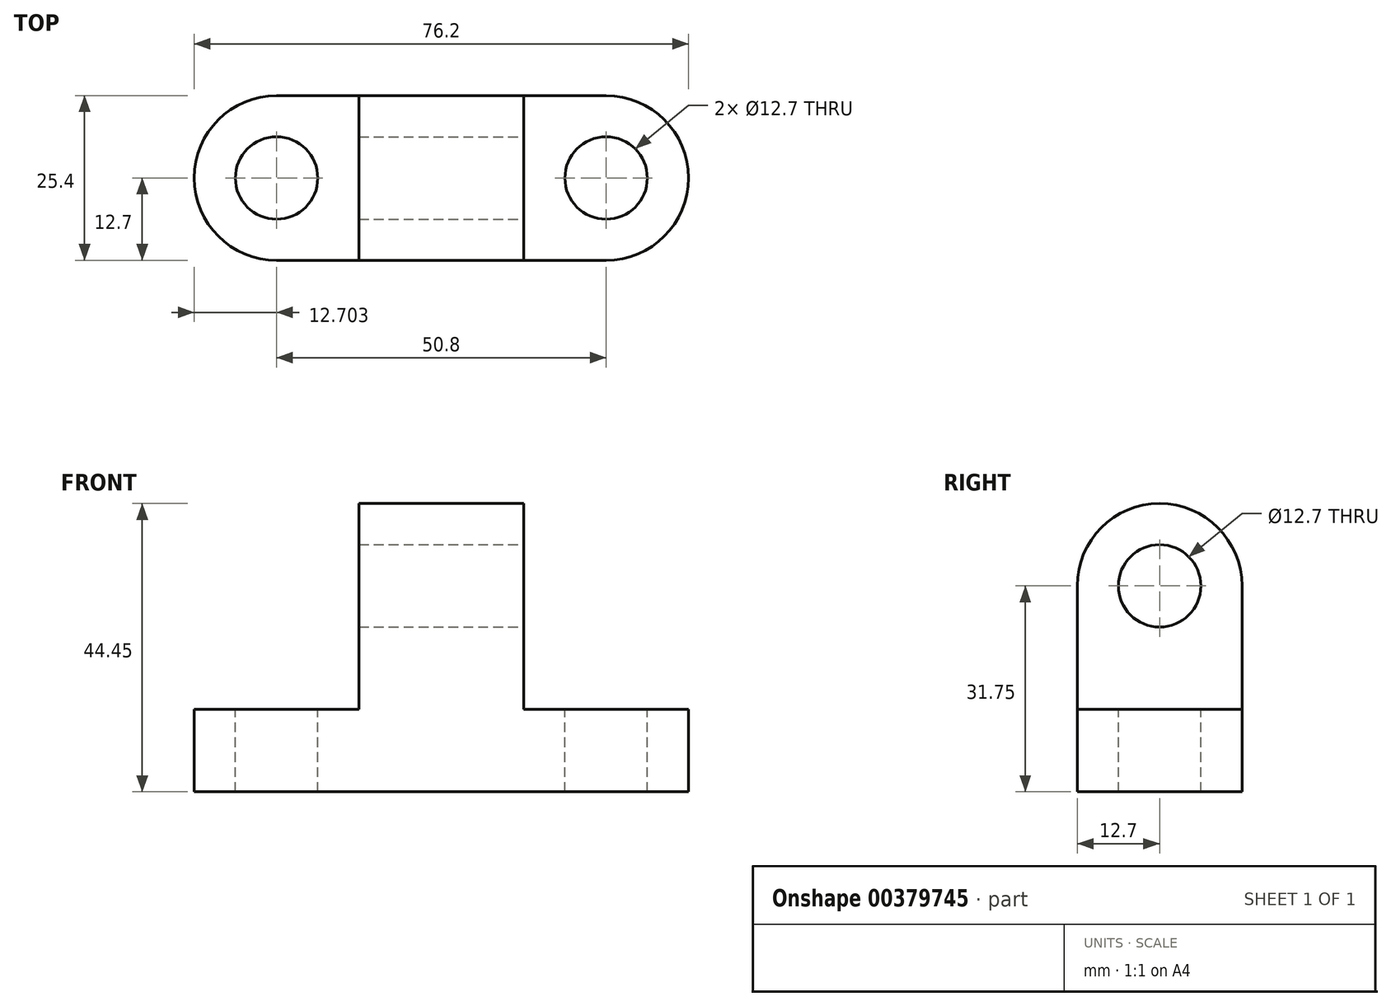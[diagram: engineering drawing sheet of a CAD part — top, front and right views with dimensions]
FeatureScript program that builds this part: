
annotation { "Feature Type Name" : "Feature", "Feature Type Description" : "" }
export const myFeature = defineFeature(function(context is Context, id is Id, definition is map)
    precondition{}
    {
        {
            var Q0;
            Q0=qCreatedBy(makeId("Front.planeOp"),FACE);
            var sketch = newSketch(context, id + "F0", { "sketchPlane" : qUnion([Q0])});
            skLineSegment(sketch, "E0", {"start": v(-34.46, 0) * mm, "end": v(41.74, 0) * mm});
            skLineSegment(sketch, "E1", {"start": v(41.74, 0) * mm, "end": v(41.74, 12.7) * mm});
            skLineSegment(sketch, "E2", {"start": v(41.74, 12.7) * mm, "end": v(16.34, 12.7) * mm});
            skLineSegment(sketch, "E3", {"start": v(16.34, 12.7) * mm, "end": v(16.34, 44.45) * mm});
            skLineSegment(sketch, "E4", {"start": v(16.34, 44.45) * mm, "end": v(-9.06, 44.45) * mm});
            skLineSegment(sketch, "E5", {"start": v(-9.06, 44.45) * mm, "end": v(-9.06, 12.7) * mm});
            skLineSegment(sketch, "E6", {"start": v(-9.06, 12.7) * mm, "end": v(-34.46, 12.7) * mm});
            skLineSegment(sketch, "E7", {"start": v(-34.46, 12.7) * mm, "end": v(-34.46, 0) * mm});
            skSolve(sketch);
        }
        {
            var Q0;
            Q0 = qSketchRegion(id + "F0", true);
            extrude(context, id + "F1", {"entities" : qUnion([Q0]), "depth" : 25.4 * mm});
        }
        {
            var Q0;
            Q0=makeQuery(id+"F1.opExtrude","CAP_EDGE",EDGE,{"disambiguationData":[OSD([sQuery(id+"F0.wireOp",EDGE,"E1")])],"isStart":false});
            fillet(context, id + "F2", {"entities" : qUnion([Q0]), "radius" : 12.7 * mm, "tangentPropagation" : true, "allowEdgeOverflow" : false});
        }
        {
            var Q0;
            Q0=makeQuery(id+"F1.opExtrude","CAP_EDGE",EDGE,{"disambiguationData":[OSD([sQuery(id+"F0.wireOp",EDGE,"E1")])],"isStart":true});
            fillet(context, id + "F3", {"entities" : qUnion([Q0]), "radius" : 12.7 * mm, "tangentPropagation" : true, "allowEdgeOverflow" : false});
        }
        {
            var Q0;
            Q0=makeQuery(id+"F1.opExtrude","CAP_EDGE",EDGE,{"disambiguationData":[OSD([sQuery(id+"F0.wireOp",EDGE,"E7")])],"isStart":false});
            fillet(context, id + "F4", {"entities" : qUnion([Q0]), "radius" : 12.7 * mm, "tangentPropagation" : true, "allowEdgeOverflow" : false});
        }
        {
            var Q0;
            Q0=makeQuery(id+"F1.opExtrude","CAP_EDGE",EDGE,{"disambiguationData":[OSD([sQuery(id+"F0.wireOp",EDGE,"E7")])],"isStart":true});
            fillet(context, id + "F5", {"entities" : qUnion([Q0]), "radius" : 12.7 * mm, "tangentPropagation" : true, "allowEdgeOverflow" : false});
        }
        {
            var Q0;
            Q0=makeQuery(id+"F1.opExtrude","CAP_EDGE",EDGE,{"disambiguationData":[OSD([sQuery(id+"F0.wireOp",EDGE,"E4")])],"isStart":false});
            fillet(context, id + "F6", {"entities" : qUnion([Q0]), "radius" : 12.7 * mm, "tangentPropagation" : true, "allowEdgeOverflow" : false});
        }
        {
            var Q0;
            Q0=makeQuery(id+"F1.opExtrude","CAP_EDGE",EDGE,{"disambiguationData":[OSD([sQuery(id+"F0.wireOp",EDGE,"E4")])],"isStart":true});
            fillet(context, id + "F7", {"entities" : qUnion([Q0]), "radius" : 12.7 * mm, "tangentPropagation" : true, "allowEdgeOverflow" : false});
        }
        {
            var Q0;
            Q0=makeQuery(id+"F1.opExtrude","SWEPT_FACE",FACE,{"disambiguationData":[OSD([sQuery(id+"F0.wireOp",EDGE,"E2")])]});
            var sketch = newSketch(context, id + "F8", { "sketchPlane" : qUnion([Q0])});
            skCircle(sketch, "E8", {"center": v(29.04, -12.7) * mm, "radius": 6.35 * mm});
            skSolve(sketch);
        }
        {
            var Q0;
            Q0 = qSketchRegion(id + "F8", true);
            extrude(context, id + "F9", {"entities" : qUnion([Q0]), "operationType" : NewBodyOperationType.REMOVE, "oppositeDirection" : true, "depth" : 25.4 * mm});
        }
        {
            var Q0;
            Q0=makeQuery(id+"F1.opExtrude","SWEPT_FACE",FACE,{"disambiguationData":[OSD([sQuery(id+"F0.wireOp",EDGE,"E6")])]});
            var sketch = newSketch(context, id + "F10", { "sketchPlane" : qUnion([Q0])});
            skCircle(sketch, "E9", {"center": v(-21.76, -12.7) * mm, "radius": 6.35 * mm});
            skSolve(sketch);
        }
        {
            var Q0;
            Q0 = qSketchRegion(id + "F10", true);
            extrude(context, id + "F11", {"entities" : qUnion([Q0]), "operationType" : NewBodyOperationType.REMOVE, "oppositeDirection" : true, "depth" : 25.4 * mm});
        }
        {
            var Q0;
            Q0=makeQuery(id+"F1.opExtrude","SWEPT_FACE",FACE,{"disambiguationData":[OSD([sQuery(id+"F0.wireOp",EDGE,"E3")])]});
            var sketch = newSketch(context, id + "F12", { "sketchPlane" : qUnion([Q0])});
            skCircle(sketch, "E10", {"center": v(-12.7, 31.75) * mm, "radius": 6.35 * mm});
            skSolve(sketch);
        }
        {
            var Q0;
            Q0 = qSketchRegion(id + "F12", true);
            extrude(context, id + "F13", {"entities" : qUnion([Q0]), "operationType" : NewBodyOperationType.REMOVE, "oppositeDirection" : true, "depth" : 25.4 * mm});
        }
    });
